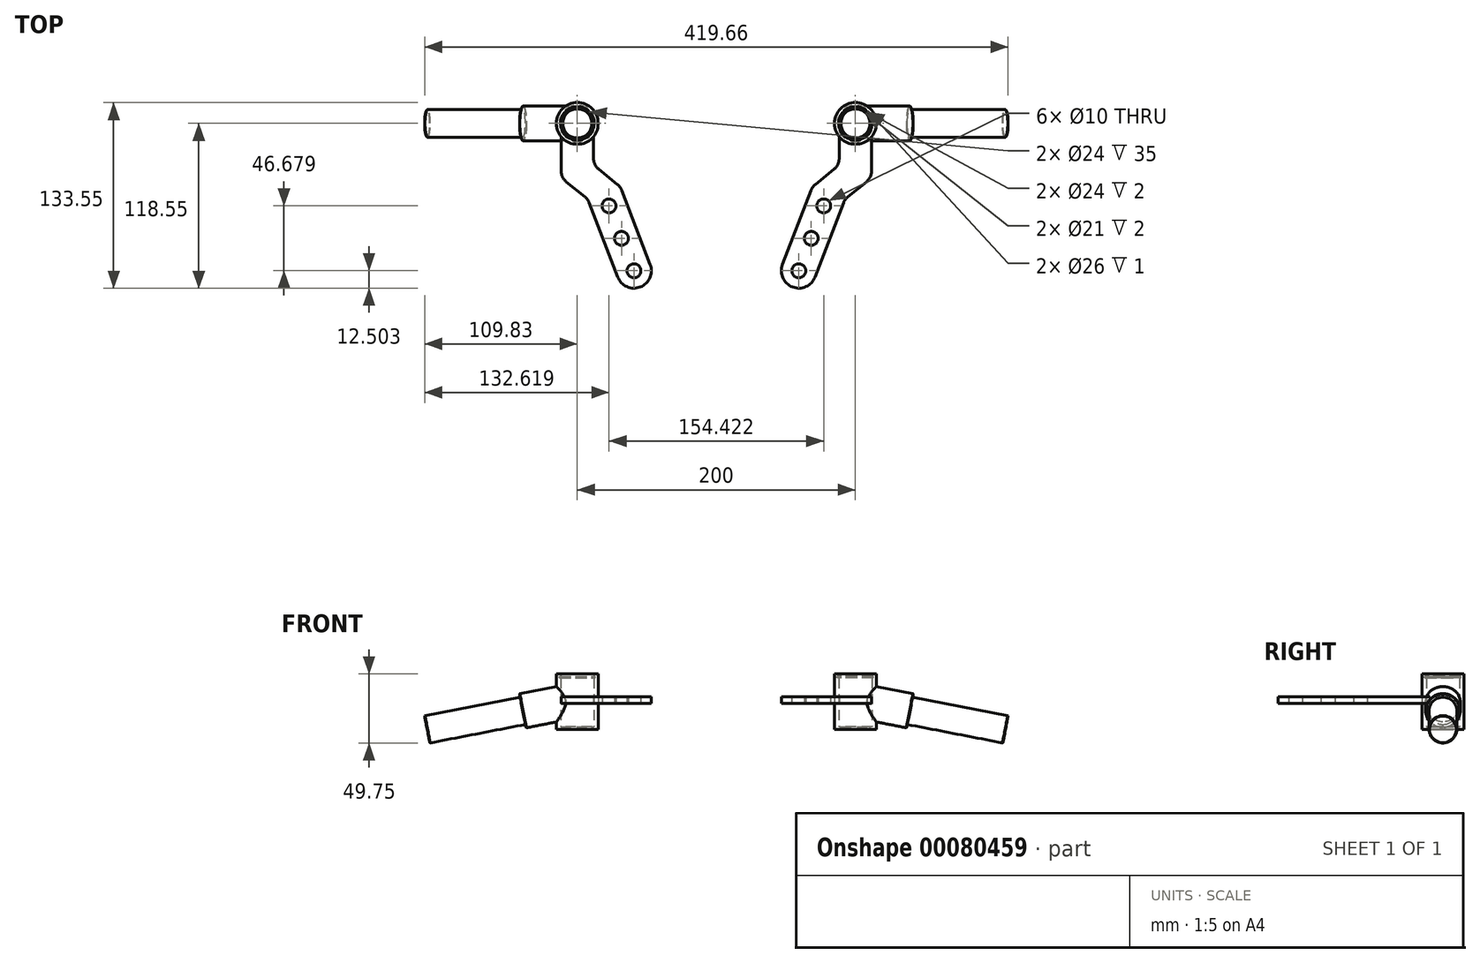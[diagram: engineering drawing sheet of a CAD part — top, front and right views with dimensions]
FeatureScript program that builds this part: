
annotation { "Feature Type Name" : "Feature", "Feature Type Description" : "" }
export const myFeature = defineFeature(function(context is Context, id is Id, definition is map)
    precondition{}
    {
        {
            var Q0;
            Q0=qCreatedBy(makeId("Top.planeOp"),FACE);
            var sketch = newSketch(context, id + "F0", { "sketchPlane" : qUnion([Q0])});
            skCircle(sketch, "E0", {"center": v(0, 0) * mm, "radius": 15 * mm});
            skCircle(sketch, "E1", {"center": v(0, 0) * mm, "radius": 12 * mm});
            skSolve(sketch);
        }
        {
            var Q0;
            Q0 = qSketchRegion(id + "F0", true);
            extrude(context, id + "F1", {"entities" : qUnion([Q0]), "depth" : 38 * mm, "symmetric" : true});
        }
        {
            var Q0;
            Q0=makeQuery(id+"F1.opExtrude","CAP_FACE",FACE,{"disambiguationData":[OSD([sQuery(id+"F0.wireOp",EDGE,"E0"),sQuery(id+"F0.wireOp",EDGE,"E1")])],"isStart":true});
            var sketch = newSketch(context, id + "F2", { "sketchPlane" : qUnion([Q0])});
            skCircle(sketch, "E2.0", {"center": v(0, 0) * mm, "radius": 15 * mm});
            skCircle(sketch, "E3", {"center": v(0, 0) * mm, "radius": 10.5 * mm});
            skSolve(sketch);
        }
        {
            var Q0;
            Q0 = qSketchRegion(id + "F2", true);
            extrude(context, id + "F3", {"entities" : qUnion([Q0]), "operationType" : NewBodyOperationType.ADD, "depth" : 2 * mm});
        }
        {
            var Q0;
            Q0=qCreatedBy(makeId("Front.planeOp"),FACE);
            var sketch = newSketch(context, id + "F4", { "sketchPlane" : qUnion([Q0])});
            skLineSegment(sketch, "E4.bottom", {"start": v(11, 17) * mm, "end": v(13, 17) * mm});
            skLineSegment(sketch, "E4.top", {"start": v(11, 16) * mm, "end": v(13, 16) * mm});
            skLineSegment(sketch, "E4.left", {"start": v(11, 17) * mm, "end": v(11, 16) * mm});
            skLineSegment(sketch, "E4.right", {"start": v(13, 17) * mm, "end": v(13, 16) * mm});
            skLineSegment(sketch, "E5", {"start": v(0, 0) * mm, "end": v(0, 17.33) * mm, "construction": true});
            skSolve(sketch);
        }
        {
            var Q0;
            Q0 = qSketchRegion(id + "F4", true);
            var Q1;
            Q1=sQuery(id+"F4.wireOp",EDGE,"E5");
            revolve(context, id + "F5", {"operationType" : NewBodyOperationType.REMOVE, "entities" : qUnion([Q0]), "axis" : qUnion([Q1]), "revolveType" : RevolveType.FULL, "oppositeDirection" : true});
        }
        {
            var Q0;
            Q0=qCreatedBy(makeId("Right.planeOp"),FACE);
            cPlane(context, id + "F6", {"entities" : qUnion([Q0]), "cplaneType" : CPlaneType.OFFSET, "offset" : 40 * mm, "width" : 150 * mm, "height" : 150 * mm});
        }
        {
            var Q0;
            Q0=qCreatedBy(id+"F6.planeOp",FACE);
            var sketch = newSketch(context, id + "F7", { "sketchPlane" : qUnion([Q0])});
            skCircle(sketch, "E6", {"center": v(0, 0) * mm, "radius": 10 * mm});
            skSolve(sketch);
        }
        {
            var Q0;
            Q0 = qSketchRegion(id + "F7", true);
            extrude(context, id + "F8", {"entities" : qUnion([Q0]), "depth" : 70 * mm});
        }
        {
            var Q0;
            Q0=qCreatedBy(makeId("Top.planeOp"),FACE);
            var sketch = newSketch(context, id + "F9", { "sketchPlane" : qUnion([Q0])});
            skLineSegment(sketch, "E7", {"start": v(0, 0) * mm, "end": v(0, -97.15) * mm});
            skSolve(sketch);
        }
        {
            var Q0;
            Q0=makeQuery(id+"F8.opExtrude","SWEPT_BODY",BODY,{"disambiguationData":[OSD([sQuery(id+"F7.wireOp",EDGE,"E6")])]});
            var Q1;
            Q1=sQuery(id+"F9.wireOp",EDGE,"E7");
            transform(context, id + "F10", {"entities" : qUnion([Q0]), "transformType" : TransformType.ROTATION, "transformAxis" : qUnion([Q1]), "angle" : 11 * degree, "oppositeDirection" : true, "makeCopy" : false});
        }
        {
            var Q0;
            Q0=makeQuery(id+"F8.opExtrude","CAP_FACE",FACE,{"disambiguationData":[OSD([sQuery(id+"F7.wireOp",EDGE,"E6")])],"isStart":true});
            var sketch = newSketch(context, id + "F11", { "sketchPlane" : qUnion([Q0])});
            skCircle(sketch, "E8", {"center": v(0, 0) * mm, "radius": 12.5 * mm});
            skSolve(sketch);
        }
        {
            var Q0;
            Q0 = qSketchRegion(id + "F11", true);
            var Q1;
            Q1=makeQuery(id+"F3.boolean.opBoolean","MERGE",FACE,{"derivedFrom":[makeQuery(id+"F1.opExtrude","SWEPT_FACE",FACE,{"disambiguationData":[OSD([sQuery(id+"F0.wireOp",EDGE,"E0")])]}),makeQuery(id+"F3.opExtrude","SWEPT_FACE",FACE,{"disambiguationData":[OSD([sQuery(id+"F2.wireOp",EDGE,"E2.0")])]})]});
            extrude(context, id + "F12", {"entities" : qUnion([Q0]), "operationType" : NewBodyOperationType.ADD, "endBound" : BoundingType.UP_TO_SURFACE, "endBoundEntityFace" : qUnion([Q1]), "depth" : 25 * mm});
        }
        {
            var Q0;
            Q0=makeQuery(id+"F8.opExtrude","CAP_EDGE",EDGE,{"disambiguationData":[OSD([sQuery(id+"F7.wireOp",EDGE,"E6")])],"isStart":true});
            var Q1;
            Q1=makeQuery(id+"F8.opExtrude","CAP_EDGE",EDGE,{"disambiguationData":[OSD([sQuery(id+"F7.wireOp",EDGE,"E6")])],"isStart":false});
            var Q2;
            Q2=makeQuery(id+"F12.opExtrude","CAP_EDGE",EDGE,{"disambiguationData":[OSD([sQuery(id+"F11.wireOp",EDGE,"E8")])],"isStart":true});
            chamfer(context, id + "F13", {"entities" : qUnion([Q0, Q1, Q2]), "width" : 0.3 * mm, "tangentPropagation" : true});
        }
        {
            var Q0;
            Q0=qCreatedBy(makeId("Top.planeOp"),FACE);
            var sketch = newSketch(context, id + "F14", { "sketchPlane" : qUnion([Q0])});
            skLineSegment(sketch, "E9", {"start": v(0, 0) * mm, "end": v(0, -72.65) * mm, "construction": true});
            skLineSegment(sketch, "E10", {"start": v(0, 0) * mm, "end": v(-40.7, -106.05) * mm, "construction": true});
            skCircle(sketch, "E11", {"center": v(-40.7, -106.05) * mm, "radius": 5 * mm});
            skCircle(sketch, "E12", {"center": v(-31.75, -82.7) * mm, "radius": 5 * mm});
            skCircle(sketch, "E13", {"center": v(-22.79, -59.37) * mm, "radius": 5 * mm});
            skArc(sketch, "E14", {"start": v(-52.38, -101.57) * mm, "mid": v(-45.19, -117.72) * mm, "end": v(-29.04, -110.53) * mm});
            skLineSegment(sketch, "E15", {"start": v(-52.38, -101.57) * mm, "end": v(-30.88, -45.55) * mm});
            skCircle(sketch, "E16.0", {"center": v(0, 0) * mm, "radius": 15 * mm});
            skLineSegment(sketch, "E17", {"start": v(-11.67, -9.42) * mm, "end": v(-11.67, -30) * mm});
            skLineSegment(sketch, "E18", {"start": v(-11.67, -30) * mm, "end": v(-30.88, -45.55) * mm});
            skLineSegment(sketch, "E19", {"start": v(11.67, -9.42) * mm, "end": v(11.67, -38.96) * mm});
            skLineSegment(sketch, "E20", {"start": v(-29.04, -110.53) * mm, "end": v(-7.54, -54.51) * mm});
            skLineSegment(sketch, "E21", {"start": v(-7.54, -54.51) * mm, "end": v(11.67, -38.96) * mm});
            skSolve(sketch);
        }
        {
            var Q0;
            Q0=makeQuery(id+"F14.imprint","IMPRINT",FACE,{"disambiguationData":[TD([[makeQuery(id+"F14.imprint","IMPRINT",EDGE,{"derivedFrom":sQuery(id+"F14.wireOp",EDGE,"E11")}),-1.0]])]});
            extrude(context, id + "F15", {"entities" : qUnion([Q0]), "depth" : 4.8 * mm, "symmetric" : true});
        }
        {
            var Q0;
            Q0=makeQuery(id+"F15.opExtrude","SWEPT_EDGE",EDGE,{"disambiguationData":[OSD([sQuery(id+"F14.wireOp",EDGE,"E20"),sQuery(id+"F14.wireOp",EDGE,"E21")])]});
            var Q1;
            Q1=makeQuery(id+"F15.opExtrude","SWEPT_EDGE",EDGE,{"disambiguationData":[OSD([sQuery(id+"F14.wireOp",EDGE,"E19"),sQuery(id+"F14.wireOp",EDGE,"E21")])]});
            var Q2;
            Q2=makeQuery(id+"F15.opExtrude","SWEPT_EDGE",EDGE,{"disambiguationData":[OSD([sQuery(id+"F14.wireOp",EDGE,"E15"),sQuery(id+"F14.wireOp",EDGE,"E18")])]});
            var Q3;
            Q3=makeQuery(id+"F15.opExtrude","SWEPT_EDGE",EDGE,{"disambiguationData":[OSD([sQuery(id+"F14.wireOp",EDGE,"E17"),sQuery(id+"F14.wireOp",EDGE,"E18")])]});
            fillet(context, id + "F16", {"entities" : qUnion([Q0, Q1, Q2, Q3]), "radius" : 10 * mm, "tangentPropagation" : true, "allowEdgeOverflow" : false});
        }
        {
            var Q0;
            Q0=qCreatedBy(makeId("Right.planeOp"),FACE);
            cPlane(context, id + "F17", {"entities" : qUnion([Q0]), "cplaneType" : CPlaneType.OFFSET, "offset" : 100 * mm, "oppositeDirection" : true, "width" : 150 * mm, "height" : 150 * mm});
        }
        {
            var Q0;
            Q0=makeQuery(id+"F8.opExtrude","SWEPT_BODY",BODY,{"disambiguationData":[OSD([sQuery(id+"F7.wireOp",EDGE,"E6")])]});
            var Q1;
            Q1=makeQuery(id+"F1.opExtrude","SWEPT_BODY",BODY,{"disambiguationData":[OSD([sQuery(id+"F0.wireOp",EDGE,"E0"),sQuery(id+"F0.wireOp",EDGE,"E1")])]});
            var Q2;
            Q2=makeQuery(id+"F15.opExtrude","SWEPT_BODY",BODY,{"disambiguationData":[OSD([sQuery(id+"F14.wireOp",EDGE,"E11"),sQuery(id+"F14.wireOp",EDGE,"E12"),sQuery(id+"F14.wireOp",EDGE,"E13"),sQuery(id+"F14.wireOp",EDGE,"E14"),sQuery(id+"F14.wireOp",EDGE,"E15"),sQuery(id+"F14.wireOp",EDGE,"E16.0"),sQuery(id+"F14.wireOp",EDGE,"E17"),sQuery(id+"F14.wireOp",EDGE,"E18"),sQuery(id+"F14.wireOp",EDGE,"E19"),sQuery(id+"F14.wireOp",EDGE,"E20"),sQuery(id+"F14.wireOp",EDGE,"E21")])]});
            var Q3;
            Q3=qCreatedBy(id+"F17.planeOp",FACE);
            mirror(context, id + "F18", {"entities" : qUnion([Q0, Q1, Q2]), "mirrorPlane" : qUnion([Q3])});
        }
    });
